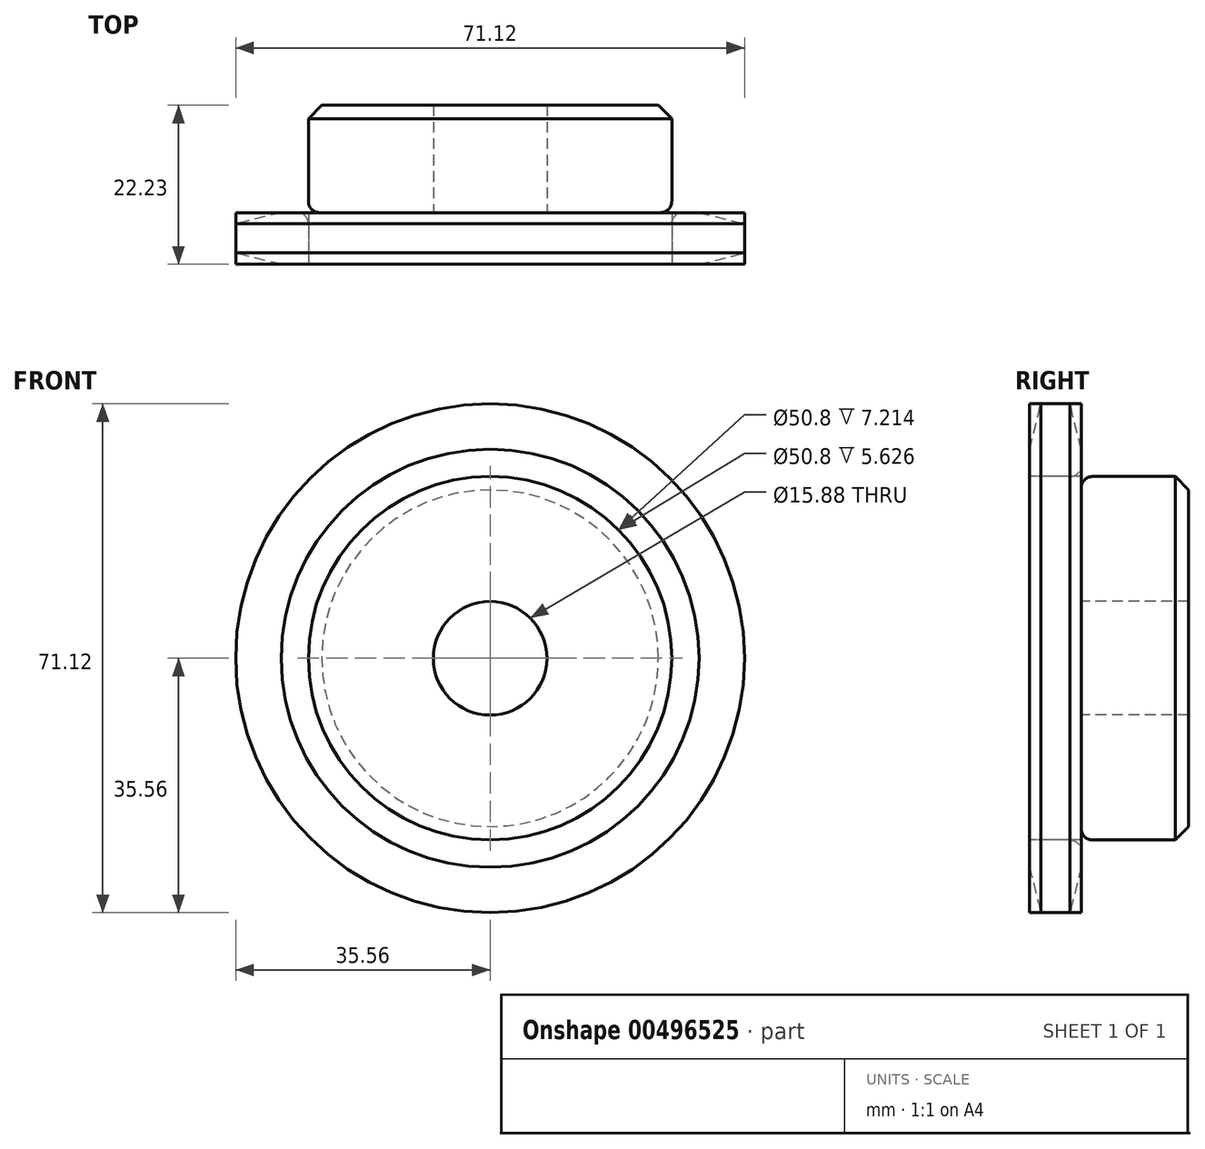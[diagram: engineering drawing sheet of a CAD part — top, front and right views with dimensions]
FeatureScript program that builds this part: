
annotation { "Feature Type Name" : "Feature", "Feature Type Description" : "" }
export const myFeature = defineFeature(function(context is Context, id is Id, definition is map)
    precondition{}
    {
        {
            var Q0;
            Q0=qCreatedBy(makeId("Right.planeOp"),FACE);
            var sketch = newSketch(context, id + "F0", { "sketchPlane" : qUnion([Q0])});
            skLineSegment(sketch, "E0", {"start": v(22.23, 0) * mm, "end": v(0, 0) * mm, "construction": true});
            skLineSegment(sketch, "E1.bottom", {"start": v(0, 7.94) * mm, "end": v(7.21, 7.94) * mm});
            skLineSegment(sketch, "E1.top", {"start": v(0, 35.56) * mm, "end": v(7.21, 35.56) * mm});
            skLineSegment(sketch, "E1.left", {"start": v(0, 7.94) * mm, "end": v(0, 35.56) * mm});
            skLineSegment(sketch, "E1.right", {"start": v(7.21, 7.94) * mm, "end": v(7.21, 35.56) * mm});
            skLineSegment(sketch, "E2.bottom", {"start": v(0, 7.94) * mm, "end": v(22.23, 7.94) * mm});
            skLineSegment(sketch, "E2.top", {"start": v(0, 25.4) * mm, "end": v(22.23, 25.4) * mm});
            skLineSegment(sketch, "E2.left", {"start": v(0, 7.94) * mm, "end": v(0, 25.4) * mm});
            skLineSegment(sketch, "E2.right", {"start": v(22.23, 7.94) * mm, "end": v(22.22, 25.4) * mm});
            skLineSegment(sketch, "E3.MirrorCS", {"start": v(0, -7.94) * mm, "end": v(7.21, -7.94) * mm});
            skLineSegment(sketch, "E4.MirrorCS", {"start": v(0, -35.56) * mm, "end": v(7.21, -35.56) * mm});
            skLineSegment(sketch, "E5.MirrorCS", {"start": v(0, -7.94) * mm, "end": v(0, -35.56) * mm});
            skLineSegment(sketch, "E6.MirrorCS", {"start": v(0, -25.4) * mm, "end": v(22.23, -25.4) * mm});
            skLineSegment(sketch, "E7.MirrorCS", {"start": v(7.21, -7.94) * mm, "end": v(7.21, -35.56) * mm});
            skLineSegment(sketch, "E8.MirrorCS", {"start": v(22.23, -7.94) * mm, "end": v(22.23, -25.4) * mm});
            skLineSegment(sketch, "E9.MirrorCS", {"start": v(0, -7.94) * mm, "end": v(0, -25.4) * mm});
            skLineSegment(sketch, "E10.MirrorCS", {"start": v(0, -7.94) * mm, "end": v(22.23, -7.94) * mm});
            skSolve(sketch);
        }
        {
            var Q0;
            {var subQ0=sQuery(id+"F0.wireOp",EDGE,"E1.top");Q0=makeQuery(id+"F0.imprint","IMPRINT",FACE,{"disambiguationData":[TD([[makeQuery(id+"F0.imprint","IMPRINT",EDGE,{"derivedFrom":subQ0}),-1.0]])]});}
            var Q1;
            {var subQ0=sQuery(id+"F0.wireOp",EDGE,"E4.MirrorCS");Q1=makeQuery(id+"F0.imprint","IMPRINT",FACE,{"disambiguationData":[TD([[makeQuery(id+"F0.imprint","IMPRINT",EDGE,{"derivedFrom":subQ0}),1.0]])]});}
            var Q2;
            {var subQ0=sQuery(id+"F0.wireOp",EDGE,"E8.MirrorCS");Q2=makeQuery(id+"F0.imprint","IMPRINT",FACE,{"disambiguationData":[TD([[makeQuery(id+"F0.imprint","IMPRINT",EDGE,{"derivedFrom":subQ0}),-1.0]])]});}
            var Q3;
            {var subQ5=sQuery(id+"F0.wireOp",EDGE,"E2.left");Q3=makeQuery(id+"F0.imprint","IMPRINT",FACE,{"disambiguationData":[TD([[makeQuery(id+"F0.imprint","IMPRINT",EDGE,{"derivedFrom":subQ5}),-1.0]])]});}
            var Q4;
            {var subQ0=sQuery(id+"F0.wireOp",EDGE,"E9.MirrorCS");Q4=makeQuery(id+"F0.imprint","IMPRINT",FACE,{"disambiguationData":[TD([[makeQuery(id+"F0.imprint","IMPRINT",EDGE,{"derivedFrom":subQ0}),1.0]])]});}
            var Q5;
            Q5=sQuery(id+"F0.wireOp",EDGE,"E0");
            revolve(context, id + "F1", {"entities" : qUnion([Q0, Q1, Q2, Q3, Q4]), "axis" : qUnion([Q5]), "revolveType" : RevolveType.FULL, "oppositeDirection" : true});
        }
        {
            var Q0;
            Q0=makeQuery(id+"F1.opRevolve","SWEPT_EDGE",EDGE,{"disambiguationData":[OSD([sQuery(id+"F0.wireOp",EDGE,"E6.MirrorCS"),sQuery(id+"F0.wireOp",EDGE,"E7.MirrorCS")])]});
            fillet(context, id + "F2", {"entities" : qUnion([Q0]), "radius" : 1.59 * mm, "tangentPropagation" : true, "allowEdgeOverflow" : false});
        }
        {
            var Q0;
            Q0=makeQuery(id+"F1.opRevolve","SWEPT_EDGE",EDGE,{"disambiguationData":[OSD([sQuery(id+"F0.wireOp",EDGE,"E6.MirrorCS"),sQuery(id+"F0.wireOp",EDGE,"E8.MirrorCS")])]});
            chamfer(context, id + "F3", {"entities" : qUnion([Q0]), "width" : 1.88 * mm, "tangentPropagation" : true});
        }
        {
            var Q0;
            Q0=makeQuery(id+"F1.opRevolve","SWEPT_EDGE",EDGE,{"disambiguationData":[OSD([sQuery(id+"F0.wireOp",EDGE,"E4.MirrorCS"),sQuery(id+"F0.wireOp",EDGE,"E5.MirrorCS")])]});
            var Q1;
            Q1=makeQuery(id+"F1.opRevolve","SWEPT_EDGE",EDGE,{"disambiguationData":[OSD([sQuery(id+"F0.wireOp",EDGE,"E4.MirrorCS"),sQuery(id+"F0.wireOp",EDGE,"E7.MirrorCS")])]});
            chamfer(context, id + "F4", {"entities" : qUnion([Q0, Q1]), "chamferType" : ChamferType.TWO_OFFSETS, "width1" : 6.35 * mm, "oppositeDirection" : false, "width2" : 1.57 * mm, "tangentPropagation" : true});
        }
    });
